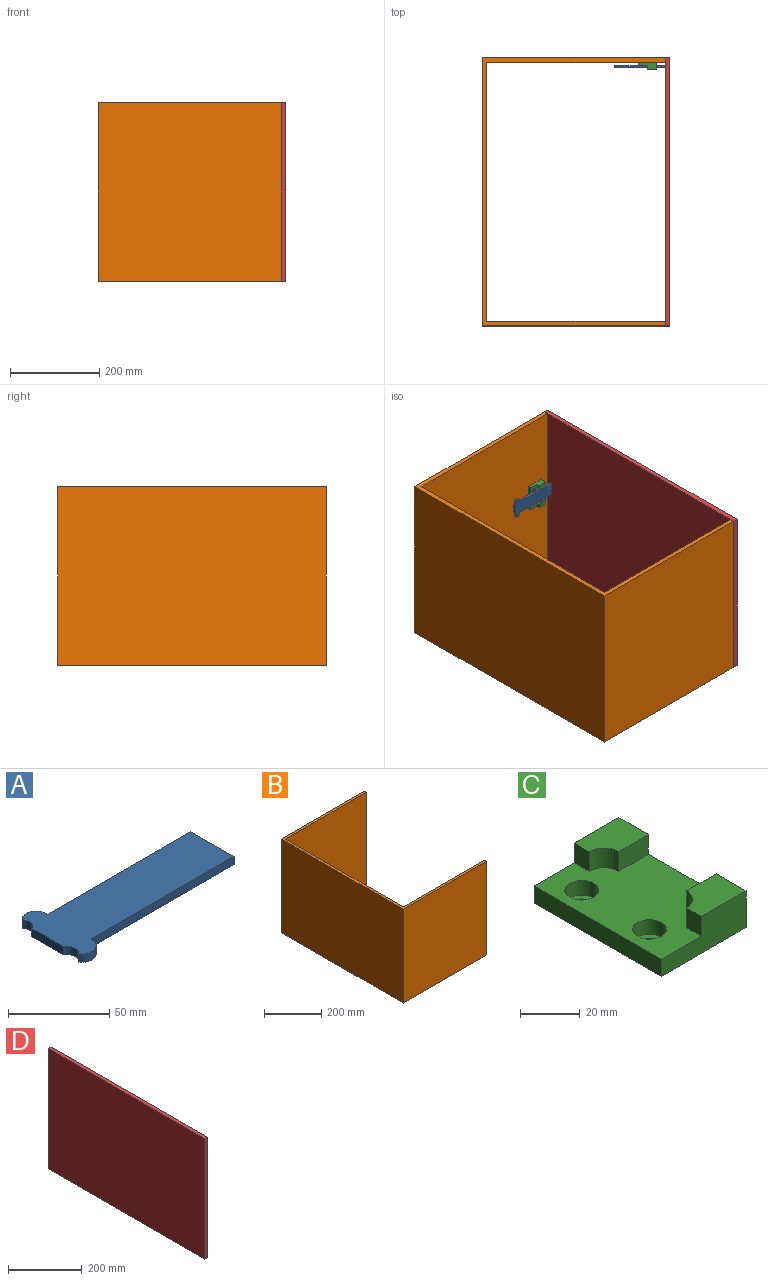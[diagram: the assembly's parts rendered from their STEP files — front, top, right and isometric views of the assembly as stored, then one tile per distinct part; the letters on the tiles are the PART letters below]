
ASSEMBLY  parts=4 mates=3
PART A: 14 faces, bbox 114x46x5 mm
  f0: plane 99.5x5mm, normal (0,1,0), area 497.5mm2, adj f1,f11,f12,f13
  f1: cylinder r=0.5mm len=5mm, axis (0,0,-1), area 3.9mm2, adj f0,f2,f12,f13
  f2: plane 5x0.5mm, normal (1,0,0), area 2.5mm2, adj f1,f3,f12,f13
  f3: cylinder r=7mm len=12.24mm, axis (0,0,-1), area 84.6mm2, adj f2,f4,f12,f13
  f4: cylinder r=5.62mm len=8.71mm, axis (0,0,-1), area 51.2mm2, adj f3,f5,f12,f13
  f5: plane 21.92x5mm, normal (-1,0,0), area 109.6mm2, adj f4,f6,f12,f13
  f6: cylinder r=5.62mm len=9.5mm, axis (0,0,-1), area 57mm2, adj f5,f7,f12,f13
  f7: cylinder r=7mm len=13.07mm, axis (0,0,-1), area 91.7mm2, adj f6,f8,f12,f13
  f8: plane 5x0.5mm, normal (1,0,0), area 2.5mm2, adj f7,f9,f12,f13
  f9: cylinder r=0.5mm len=5mm, axis (0,0,-1), area 3.9mm2, adj f8,f10,f12,f13
  f10: plane 99.5x5mm, normal (0,-1,0), area 497.5mm2, adj f9,f11,f12,f13
  f11: plane 30x5mm, normal (1,0,0), area 150mm2, adj f0,f10,f12,f13
  f12: plane 114x46mm, normal (0,0,1), area 3562.3mm2, adj f0,f1,f2,f3,f4,f5,f6,f7
  f13: plane 114x46mm, normal (0,0,-1), area 3562.3mm2, adj f0,f1,f2,f3,f4,f5,f6,f7
PART B: 10 faces, bbox 410x600x400 mm
  f0: plane 580x400mm, normal (1,0,0), area 232000mm2, adj f1,f7,f8,f9
  f1: plane 400x400mm, normal (0,-1,0), area 160000mm2, adj f0,f2,f8,f9
  f2: plane 400x10mm, normal (1,0,0), area 4000mm2, adj f1,f3,f8,f9
  f3: plane 410x400mm, normal (0,1,0), area 164000mm2, adj f2,f4,f8,f9
  f4: plane 600x400mm, normal (-1,0,0), area 240000mm2, adj f3,f5,f8,f9
  f5: plane 410x400mm, normal (0,-1,0), area 164000mm2, adj f4,f6,f8,f9
  f6: plane 400x10mm, normal (1,0,0), area 4000mm2, adj f5,f7,f8,f9
  f7: plane 400x400mm, normal (0,1,0), area 160000mm2, adj f0,f6,f8,f9
  f8: plane 600x410mm, normal (0,0,1), area 14000mm2, adj f0,f1,f2,f3,f4,f5,f6,f7
  f9: plane 600x410mm, normal (0,0,-1), area 14000mm2, adj f0,f1,f2,f3,f4,f5,f6,f7
PART C: 20 faces, bbox 40x60x15 mm
  f0: plane 60x40mm, normal (0,0,1), area 1690.2mm2, adj f1,f2,f3,f4,f6,f7,f8,f10
  f1: plane 60x7mm, normal (-1,0,0), area 420mm2, adj f0,f2,f4,f5
  f2: plane 40x15mm, normal (0,-1,0), area 448mm2, adj f0,f1,f3,f5,f12,f13
  f3: plane 60x15mm, normal (1,0,0), area 644mm2, adj f0,f2,f4,f5,f8,f9,f10,f13
  f4: plane 40x15mm, normal (0,1,0), area 448mm2, adj f0,f1,f3,f5,f6,f9
  f5: plane 60x40mm, normal (0,0,-1), area 2323mm2, adj f1,f2,f3,f4,f14,f17
  f6: plane 8x7mm, normal (-1,0,0), area 56mm2, adj f0,f4,f7,f9
  f7: cylinder r=7mm len=8mm, axis (0,0,-1), area 88mm2, adj f0,f6,f8,f9
  f8: plane 14x8mm, normal (0,-1,0), area 112mm2, adj f0,f3,f7,f9
  f9: plane 21x14mm, normal (0,0,1), area 255.5mm2, adj f3,f4,f6,f7,f8
  f10: plane 14x8mm, normal (0,1,0), area 112mm2, adj f0,f3,f11,f13
  f11: cylinder r=7mm len=8mm, axis (0,0,-1), area 88mm2, adj f0,f10,f12,f13
  f12: plane 8x7mm, normal (-1,0,0), area 56mm2, adj f0,f2,f11,f13
  f13: plane 21x14mm, normal (0,0,1), area 255.5mm2, adj f2,f3,f10,f11,f12
  f14: cylinder r=3.5mm len=7mm, axis (0,0,1), area 22mm2, adj f5,f15
  f15: plane 11.25x11.25mm, normal (0,0,1), area 60.9mm2, adj f14,f16
  f16: cylinder r=5.62mm len=11.25mm, axis (0,0,1), area 212.1mm2, adj f0,f15
  f17: cylinder r=3.5mm len=7mm, axis (0,0,1), area 22mm2, adj f5,f18
  f18: plane 11.25x11.25mm, normal (0,0,1), area 60.9mm2, adj f17,f19
  f19: cylinder r=5.62mm len=11.25mm, axis (0,0,1), area 212.1mm2, adj f0,f18
PART D: 6 faces, bbox 10x600x400 mm
  f0: plane 400x10mm, normal (0,1,0), area 4000mm2, adj f1,f3,f4,f5
  f1: plane 600x400mm, normal (-1,0,0), area 240000mm2, adj f0,f2,f4,f5
  f2: plane 400x10mm, normal (0,-1,0), area 4000mm2, adj f1,f3,f4,f5
  f3: plane 600x400mm, normal (1,0,0), area 240000mm2, adj f0,f2,f4,f5
  f4: plane 600x10mm, normal (0,0,1), area 6000mm2, adj f0,f1,f2,f3
  f5: plane 600x10mm, normal (0,0,-1), area 6000mm2, adj f0,f1,f2,f3
PLACE A rot(axis=(1,0,0),90deg) t=(-212.85,154.46,200)mm
PLACE B t=(-212.67,56.04,0)mm fixed
PLACE C rot(axis=(1,0,0),90deg) t=(-146.85,154.46,200)mm
PLACE D t=(-261.12,56.04,0)mm
MATE fastened A.f11 <-> D.f1  axis (1,0,0) through (-106.85,147.46,200)mm
MATE revolute D.f4 <-> B.f8  axis (0,0,-1) through (-106.85,-435.54,400)mm
MATE fastened C.f5 <-> B.f1  axis (0,1,0) through (-126.85,154.46,200)mm
